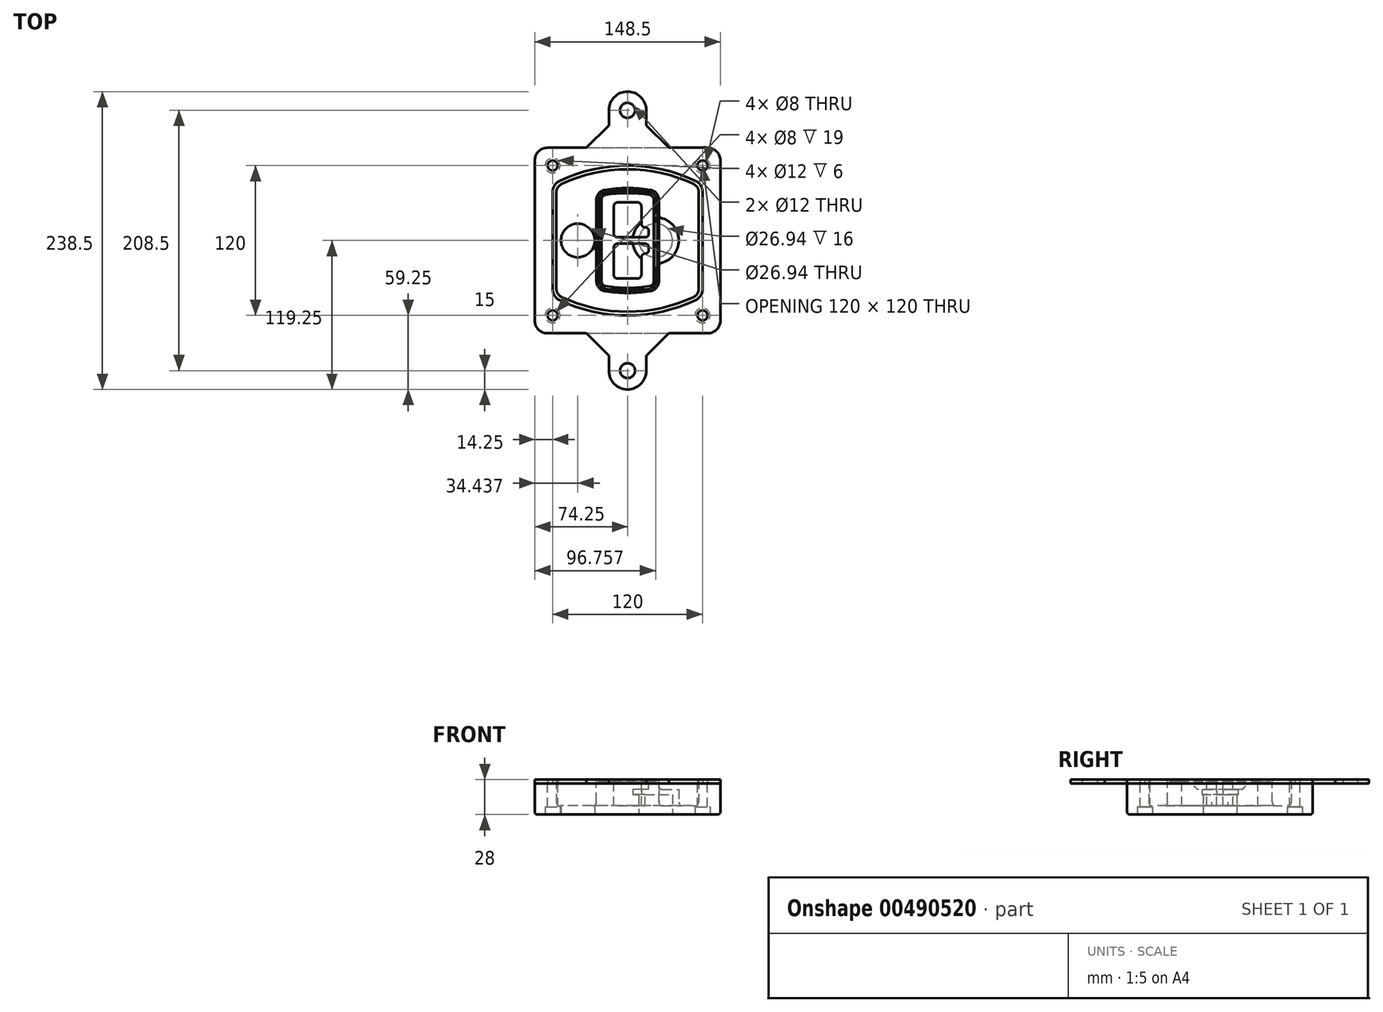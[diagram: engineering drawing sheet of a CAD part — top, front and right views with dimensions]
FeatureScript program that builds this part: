
annotation { "Feature Type Name" : "Feature", "Feature Type Description" : "" }
export const myFeature = defineFeature(function(context is Context, id is Id, definition is map)
    precondition{}
    {
        {
            var Q0;
            Q0=qCreatedBy(makeId("Top.planeOp"),FACE);
            var sketch = newSketch(context, id + "F0", { "sketchPlane" : qUnion([Q0])});
            skPoint(sketch, "E0.rect.middle", {"position": v(0, 0) * mm});
            skLineSegment(sketch, "E1.bottom", {"start": v(-64.25, -74.25) * mm, "end": v(64.25, -74.25) * mm});
            skLineSegment(sketch, "E1.top", {"start": v(-64.25, 74.25) * mm, "end": v(64.25, 74.25) * mm});
            skLineSegment(sketch, "E1.left", {"start": v(-74.25, -64.25) * mm, "end": v(-74.25, 64.25) * mm});
            skLineSegment(sketch, "E1.right", {"start": v(74.25, -64.25) * mm, "end": v(74.25, 64.25) * mm});
            skLineSegment(sketch, "E2", {"start": v(-74.25, 74.25) * mm, "end": v(74.25, -74.25) * mm, "construction": true});
            skLineSegment(sketch, "E3", {"start": v(74.25, 74.25) * mm, "end": v(-74.25, -74.25) * mm, "construction": true});
            skCircle(sketch, "E4", {"center": v(-60, 60) * mm, "radius": 4 * mm});
            skCircle(sketch, "E5", {"center": v(60, 60) * mm, "radius": 4 * mm});
            skCircle(sketch, "E6", {"center": v(60, -60) * mm, "radius": 4 * mm});
            skCircle(sketch, "E7", {"center": v(-60, -60) * mm, "radius": 4 * mm});
            skLineSegment(sketch, "E8", {"start": v(-60, 60) * mm, "end": v(60, 60) * mm, "construction": true});
            skLineSegment(sketch, "E9", {"start": v(60, 60) * mm, "end": v(60, -60) * mm, "construction": true});
            skLineSegment(sketch, "E10", {"start": v(60, -60) * mm, "end": v(-60, -60) * mm, "construction": true});
            skLineSegment(sketch, "E11", {"start": v(-60, -60) * mm, "end": v(-60, 60) * mm, "construction": true});
            skLineSegment(sketch, "E12", {"start": v(-60, 38.83) * mm, "end": v(-60, -38.83) * mm});
            skLineSegment(sketch, "E13", {"start": v(60, 38.83) * mm, "end": v(60, -38.83) * mm});
            skArc(sketch, "E14", {"start": v(54.26, 47.88) * mm, "mid": v(0, 60) * mm, "end": v(-54.26, 47.88) * mm});
            skArc(sketch, "E15", {"start": v(-54.26, -47.88) * mm, "mid": v(0, -60) * mm, "end": v(54.26, -47.88) * mm});
            skLineSegment(sketch, "E16", {"start": v(-60, 0) * mm, "end": v(60, 0) * mm, "construction": true});
            skPoint(sketch, "E17.visualSharp", {"position": v(-60, -45) * mm});
            skArc(sketch, "E17.filletArc", {"start": v(-60, -38.83) * mm, "mid": v(-58.44, -44.2) * mm, "end": v(-54.26, -47.88) * mm});
            skPoint(sketch, "E18.visualSharp", {"position": v(-60, 45) * mm});
            skArc(sketch, "E18.filletArc", {"start": v(-54.26, 47.88) * mm, "mid": v(-58.44, 44.2) * mm, "end": v(-60, 38.83) * mm});
            skPoint(sketch, "E19.visualSharp", {"position": v(60, 45) * mm});
            skArc(sketch, "E19.filletArc", {"start": v(60, 38.83) * mm, "mid": v(58.44, 44.2) * mm, "end": v(54.26, 47.88) * mm});
            skPoint(sketch, "E20.visualSharp", {"position": v(60, -45) * mm});
            skArc(sketch, "E20.filletArc", {"start": v(54.26, -47.88) * mm, "mid": v(58.44, -44.2) * mm, "end": v(60, -38.83) * mm});
            skPoint(sketch, "E21.visualSharp", {"position": v(-74.25, 74.25) * mm});
            skArc(sketch, "E21.filletArc", {"start": v(-64.25, 74.25) * mm, "mid": v(-71.32, 71.32) * mm, "end": v(-74.25, 64.25) * mm});
            skPoint(sketch, "E22.visualSharp", {"position": v(74.25, 74.25) * mm});
            skArc(sketch, "E22.filletArc", {"start": v(74.25, 64.25) * mm, "mid": v(71.32, 71.32) * mm, "end": v(64.25, 74.25) * mm});
            skPoint(sketch, "E23.visualSharp", {"position": v(74.25, -74.25) * mm});
            skArc(sketch, "E23.filletArc", {"start": v(64.25, -74.25) * mm, "mid": v(71.32, -71.32) * mm, "end": v(74.25, -64.25) * mm});
            skPoint(sketch, "E24.visualSharp", {"position": v(-74.25, -74.25) * mm});
            skArc(sketch, "E24.filletArc", {"start": v(-74.25, -64.25) * mm, "mid": v(-71.32, -71.32) * mm, "end": v(-64.25, -74.25) * mm});
            skArc(sketch, "E25.0", {"start": v(57, 38.83) * mm, "mid": v(55.9, 42.58) * mm, "end": v(52.98, 45.17) * mm});
            skLineSegment(sketch, "E25.1", {"start": v(57, 38.83) * mm, "end": v(57, -38.83) * mm});
            skArc(sketch, "E25.2", {"start": v(52.98, -45.17) * mm, "mid": v(55.9, -42.58) * mm, "end": v(57, -38.83) * mm});
            skArc(sketch, "E25.3", {"start": v(-52.98, -45.17) * mm, "mid": v(0, -57) * mm, "end": v(52.98, -45.17) * mm});
            skArc(sketch, "E25.4", {"start": v(-57, -38.83) * mm, "mid": v(-55.9, -42.58) * mm, "end": v(-52.98, -45.17) * mm});
            skArc(sketch, "E25.5", {"start": v(52.98, 45.17) * mm, "mid": v(0, 57) * mm, "end": v(-52.98, 45.17) * mm});
            skLineSegment(sketch, "E25.6", {"start": v(-57, 38.83) * mm, "end": v(-57, -38.83) * mm});
            skArc(sketch, "E25.7", {"start": v(-52.98, 45.17) * mm, "mid": v(-55.9, 42.58) * mm, "end": v(-57, 38.83) * mm});
            skArc(sketch, "E26.0", {"start": v(-55.96, 51.5) * mm, "mid": v(-61.82, 46.33) * mm, "end": v(-64, 38.83) * mm});
            skArc(sketch, "E26.1", {"start": v(55.96, 51.5) * mm, "mid": v(0, 64) * mm, "end": v(-55.96, 51.5) * mm});
            skArc(sketch, "E26.2", {"start": v(64, 38.83) * mm, "mid": v(61.82, 46.33) * mm, "end": v(55.96, 51.5) * mm});
            skLineSegment(sketch, "E26.3", {"start": v(64, 38.83) * mm, "end": v(64, -38.83) * mm});
            skArc(sketch, "E26.4", {"start": v(55.96, -51.5) * mm, "mid": v(61.82, -46.33) * mm, "end": v(64, -38.83) * mm});
            skLineSegment(sketch, "E26.5", {"start": v(-64, 38.83) * mm, "end": v(-64, -38.83) * mm});
            skArc(sketch, "E26.6", {"start": v(-55.96, -51.5) * mm, "mid": v(0, -64) * mm, "end": v(55.96, -51.5) * mm});
            skArc(sketch, "E26.7", {"start": v(-64, -38.83) * mm, "mid": v(-61.82, -46.33) * mm, "end": v(-55.96, -51.5) * mm});
            skSolve(sketch);
        }
        {
            var Q0;
            Q0=makeQuery(id+"F0.imprint","IMPRINT",FACE,{"disambiguationData":[TD([[makeQuery(id+"F0.imprint","IMPRINT",EDGE,{"derivedFrom":sQuery(id+"F0.wireOp",EDGE,"E1.bottom")}),1.0]])]});
            var Q1;
            Q1=makeQuery(id+"F0.imprint","IMPRINT",FACE,{"disambiguationData":[TD([[makeQuery(id+"F0.imprint","IMPRINT",EDGE,{"derivedFrom":sQuery(id+"F0.wireOp",EDGE,"E12")}),1.0]])]});
            var Q2;
            Q2=makeQuery(id+"F0.imprint","IMPRINT",FACE,{"disambiguationData":[TD([[makeQuery(id+"F0.imprint","IMPRINT",EDGE,{"derivedFrom":sQuery(id+"F0.wireOp",EDGE,"E25.0")}),1.0]])]});
            var Q3;
            Q3=makeQuery(id+"F0.imprint","IMPRINT",FACE,{"disambiguationData":[TD([[makeQuery(id+"F0.imprint","IMPRINT",EDGE,{"derivedFrom":sQuery(id+"F0.wireOp",EDGE,"E12")}),-1.0]])]});
            extrude(context, id + "F1", {"entities" : qUnion([Q0, Q1, Q2, Q3]), "oppositeDirection" : true, "depth" : 25 * mm});
        }
        {
            var Q0;
            Q0=makeQuery(id+"F0.imprint","IMPRINT",FACE,{"disambiguationData":[TD([[makeQuery(id+"F0.imprint","IMPRINT",EDGE,{"derivedFrom":sQuery(id+"F0.wireOp",EDGE,"E12")}),1.0]])]});
            extrude(context, id + "F2", {"entities" : qUnion([Q0]), "operationType" : NewBodyOperationType.ADD, "depth" : 3 * mm});
        }
        {
            var Q0;
            Q0=makeQuery(id+"F0.imprint","IMPRINT",FACE,{"disambiguationData":[TD([[makeQuery(id+"F0.imprint","IMPRINT",EDGE,{"derivedFrom":sQuery(id+"F0.wireOp",EDGE,"E25.0")}),1.0]])]});
            extrude(context, id + "F3", {"entities" : qUnion([Q0]), "operationType" : NewBodyOperationType.REMOVE, "oppositeDirection" : true, "depth" : 18 * mm});
        }
        {
            var Q0;
            Q0=makeQuery(id+"F2.opExtrude","CAP_FACE",FACE,{"disambiguationData":[OSD([sQuery(id+"F0.wireOp",EDGE,"E12"),sQuery(id+"F0.wireOp",EDGE,"E13"),sQuery(id+"F0.wireOp",EDGE,"E14"),sQuery(id+"F0.wireOp",EDGE,"E15"),sQuery(id+"F0.wireOp",EDGE,"E17.filletArc"),sQuery(id+"F0.wireOp",EDGE,"E18.filletArc"),sQuery(id+"F0.wireOp",EDGE,"E19.filletArc"),sQuery(id+"F0.wireOp",EDGE,"E20.filletArc"),sQuery(id+"F0.wireOp",EDGE,"E25.0"),sQuery(id+"F0.wireOp",EDGE,"E25.1"),sQuery(id+"F0.wireOp",EDGE,"E25.2"),sQuery(id+"F0.wireOp",EDGE,"E25.3"),sQuery(id+"F0.wireOp",EDGE,"E25.4"),sQuery(id+"F0.wireOp",EDGE,"E25.5"),sQuery(id+"F0.wireOp",EDGE,"E25.6"),sQuery(id+"F0.wireOp",EDGE,"E25.7")])],"isStart":false});
            var sketch = newSketch(context, id + "F4", { "sketchPlane" : qUnion([Q0])});
            skArc(sketch, "E27.0", {"start": v(-18.34, -40.45) * mm, "mid": v(0, -42) * mm, "end": v(18.34, -40.45) * mm});
            skArc(sketch, "E28.0", {"start": v(18.34, 40.45) * mm, "mid": v(0, 42) * mm, "end": v(-18.34, 40.45) * mm});
            skLineSegment(sketch, "E29", {"start": v(-25, 32.57) * mm, "end": v(-25, -32.57) * mm});
            skLineSegment(sketch, "E30", {"start": v(25, 32.57) * mm, "end": v(25, -32.57) * mm});
            skLineSegment(sketch, "E31", {"start": v(-25, 39.1) * mm, "end": v(25, 39.1) * mm, "construction": true});
            skLineSegment(sketch, "E32", {"start": v(-25, -39.1) * mm, "end": v(25, -39.1) * mm, "construction": true});
            skPoint(sketch, "E33.visualSharp", {"position": v(-25, 39.1) * mm});
            skArc(sketch, "E33.filletArc", {"start": v(-18.34, 40.45) * mm, "mid": v(-23.11, 37.73) * mm, "end": v(-25, 32.57) * mm});
            skPoint(sketch, "E34.visualSharp", {"position": v(25, 39.1) * mm});
            skArc(sketch, "E34.filletArc", {"start": v(25, 32.57) * mm, "mid": v(23.11, 37.73) * mm, "end": v(18.34, 40.45) * mm});
            skPoint(sketch, "E35.visualSharp", {"position": v(25, -39.1) * mm});
            skArc(sketch, "E35.filletArc", {"start": v(18.34, -40.45) * mm, "mid": v(23.11, -37.73) * mm, "end": v(25, -32.57) * mm});
            skPoint(sketch, "E36.visualSharp", {"position": v(-25, -39.1) * mm});
            skArc(sketch, "E36.filletArc", {"start": v(-25, -32.57) * mm, "mid": v(-23.11, -37.73) * mm, "end": v(-18.34, -40.45) * mm});
            skArc(sketch, "E37.0", {"start": v(52.98, 45.17) * mm, "mid": v(0, 57) * mm, "end": v(-52.98, 45.17) * mm});
            skArc(sketch, "E37.1", {"start": v(-52.98, 45.17) * mm, "mid": v(-55.9, 42.58) * mm, "end": v(-57, 38.83) * mm});
            skLineSegment(sketch, "E37.2", {"start": v(-57, 38.83) * mm, "end": v(-57, -38.83) * mm});
            skArc(sketch, "E37.3", {"start": v(-57, -38.83) * mm, "mid": v(-55.9, -42.58) * mm, "end": v(-52.98, -45.17) * mm});
            skArc(sketch, "E37.4", {"start": v(-52.98, -45.17) * mm, "mid": v(0, -57) * mm, "end": v(52.98, -45.17) * mm});
            skArc(sketch, "E37.5", {"start": v(52.98, -45.17) * mm, "mid": v(55.9, -42.58) * mm, "end": v(57, -38.83) * mm});
            skLineSegment(sketch, "E37.6", {"start": v(57, 38.83) * mm, "end": v(57, -38.83) * mm});
            skArc(sketch, "E37.7", {"start": v(57, 38.83) * mm, "mid": v(55.9, 42.58) * mm, "end": v(52.98, 45.17) * mm});
            skLineSegment(sketch, "E38.0", {"start": v(23, 32.57) * mm, "end": v(23, -32.57) * mm});
            skArc(sketch, "E38.1", {"start": v(18, -38.48) * mm, "mid": v(21.58, -36.44) * mm, "end": v(23, -32.57) * mm});
            skArc(sketch, "E38.2", {"start": v(-18, -38.48) * mm, "mid": v(0, -40) * mm, "end": v(18, -38.48) * mm});
            skArc(sketch, "E38.3", {"start": v(-23, -32.57) * mm, "mid": v(-21.58, -36.44) * mm, "end": v(-18, -38.48) * mm});
            skLineSegment(sketch, "E38.4", {"start": v(-23, 32.57) * mm, "end": v(-23, -32.57) * mm});
            skArc(sketch, "E38.5", {"start": v(23, 32.57) * mm, "mid": v(21.58, 36.44) * mm, "end": v(18, 38.48) * mm});
            skArc(sketch, "E38.6", {"start": v(-18, 38.48) * mm, "mid": v(-21.58, 36.44) * mm, "end": v(-23, 32.57) * mm});
            skArc(sketch, "E38.7", {"start": v(18, 38.48) * mm, "mid": v(0, 40) * mm, "end": v(-18, 38.48) * mm});
            skArc(sketch, "E39.0", {"start": v(21, 32.57) * mm, "mid": v(20.06, 35.15) * mm, "end": v(17.67, 36.5) * mm});
            skLineSegment(sketch, "E39.1", {"start": v(21, 32.57) * mm, "end": v(21, -32.57) * mm});
            skArc(sketch, "E39.2", {"start": v(17.67, -36.5) * mm, "mid": v(20.06, -35.15) * mm, "end": v(21, -32.57) * mm});
            skArc(sketch, "E39.3", {"start": v(-17.67, -36.5) * mm, "mid": v(0, -38) * mm, "end": v(17.67, -36.5) * mm});
            skArc(sketch, "E39.4", {"start": v(-21, -32.57) * mm, "mid": v(-20.06, -35.15) * mm, "end": v(-17.67, -36.5) * mm});
            skArc(sketch, "E39.5", {"start": v(17.67, 36.5) * mm, "mid": v(0, 38) * mm, "end": v(-17.67, 36.5) * mm});
            skLineSegment(sketch, "E39.6", {"start": v(-21, 32.57) * mm, "end": v(-21, -32.57) * mm});
            skArc(sketch, "E39.7", {"start": v(-17.67, 36.5) * mm, "mid": v(-20.06, 35.15) * mm, "end": v(-21, 32.57) * mm});
            skLineSegment(sketch, "E40", {"start": v(-25, 0) * mm, "end": v(25, 0) * mm, "construction": true});
            skLineSegment(sketch, "E41", {"start": v(-11, 5.5) * mm, "end": v(-11, 27.5) * mm});
            skLineSegment(sketch, "E42", {"start": v(-8, 30.5) * mm, "end": v(8, 30.5) * mm});
            skLineSegment(sketch, "E43", {"start": v(11, 27.5) * mm, "end": v(11, 13.5) * mm});
            skLineSegment(sketch, "E44", {"start": v(14, 10.5) * mm, "end": v(14, 10.5) * mm});
            skLineSegment(sketch, "E45", {"start": v(17, 7.5) * mm, "end": v(17, 5.5) * mm});
            skLineSegment(sketch, "E46", {"start": v(14, 2.5) * mm, "end": v(-8, 2.5) * mm});
            skPoint(sketch, "E47.visualSharp", {"position": v(-11, 30.5) * mm});
            skArc(sketch, "E47.filletArc", {"start": v(-8, 30.5) * mm, "mid": v(-10.12, 29.62) * mm, "end": v(-11, 27.5) * mm});
            skPoint(sketch, "E48.visualSharp", {"position": v(11, 30.5) * mm});
            skArc(sketch, "E48.filletArc", {"start": v(11, 27.5) * mm, "mid": v(10.12, 29.62) * mm, "end": v(8, 30.5) * mm});
            skPoint(sketch, "E49.visualSharp", {"position": v(11, 10.5) * mm});
            skArc(sketch, "E49.filletArc", {"start": v(11, 13.5) * mm, "mid": v(11.88, 11.38) * mm, "end": v(14, 10.5) * mm});
            skPoint(sketch, "E50.visualSharp", {"position": v(17, 10.5) * mm});
            skArc(sketch, "E50.filletArc", {"start": v(17, 7.5) * mm, "mid": v(16.12, 9.62) * mm, "end": v(14, 10.5) * mm});
            skPoint(sketch, "E51.visualSharp", {"position": v(17, 2.5) * mm});
            skArc(sketch, "E51.filletArc", {"start": v(14, 2.5) * mm, "mid": v(16.12, 3.38) * mm, "end": v(17, 5.5) * mm});
            skPoint(sketch, "E52.visualSharp", {"position": v(-11, 2.5) * mm});
            skArc(sketch, "E52.filletArc", {"start": v(-11, 5.5) * mm, "mid": v(-10.12, 3.38) * mm, "end": v(-8, 2.5) * mm});
            skLineSegment(sketch, "E53.0.MirrorCS", {"start": v(14, -2.5) * mm, "end": v(-8, -2.5) * mm});
            skArc(sketch, "E54.0.MirrorCS", {"start": v(-11, -5.5) * mm, "mid": v(-10.12, -3.38) * mm, "end": v(-8, -2.5) * mm});
            skLineSegment(sketch, "E55.0.MirrorCS", {"start": v(-11, -5.5) * mm, "end": v(-11, -27.5) * mm});
            skArc(sketch, "E56.0.MirrorCS", {"start": v(-8, -30.5) * mm, "mid": v(-10.12, -29.62) * mm, "end": v(-11, -27.5) * mm});
            skLineSegment(sketch, "E57.0.MirrorCS", {"start": v(-8, -30.5) * mm, "end": v(8, -30.5) * mm});
            skArc(sketch, "E58.0.MirrorCS", {"start": v(11, -27.5) * mm, "mid": v(10.12, -29.62) * mm, "end": v(8, -30.5) * mm});
            skLineSegment(sketch, "E59.0.MirrorCS", {"start": v(11, -27.5) * mm, "end": v(11, -13.5) * mm});
            skArc(sketch, "E60.0.MirrorCS", {"start": v(11, -13.5) * mm, "mid": v(11.88, -11.38) * mm, "end": v(14, -10.5) * mm});
            skArc(sketch, "E61.0.MirrorCS", {"start": v(17, -7.5) * mm, "mid": v(16.12, -9.62) * mm, "end": v(14, -10.5) * mm});
            skLineSegment(sketch, "E62.0.MirrorCS", {"start": v(17, -7.5) * mm, "end": v(17, -5.5) * mm});
            skArc(sketch, "E63.0.MirrorCS", {"start": v(14, -2.5) * mm, "mid": v(16.12, -3.38) * mm, "end": v(17, -5.5) * mm});
            skSolve(sketch);
        }
        {
            var Q0;
            Q0=makeQuery(id+"F4.imprint","IMPRINT",FACE,{"disambiguationData":[TD([[makeQuery(id+"F4.imprint","IMPRINT",EDGE,{"derivedFrom":sQuery(id+"F4.wireOp",EDGE,"E27.0")}),1.0]])]});
            var Q1;
            Q1=makeQuery(id+"F4.imprint","IMPRINT",FACE,{"disambiguationData":[TD([[makeQuery(id+"F4.imprint","IMPRINT",EDGE,{"derivedFrom":sQuery(id+"F4.wireOp",EDGE,"E38.0")}),-1.0]])]});
            var Q2;
            Q2=makeQuery(id+"F4.imprint","IMPRINT",FACE,{"disambiguationData":[TD([[makeQuery(id+"F4.imprint","IMPRINT",EDGE,{"derivedFrom":sQuery(id+"F4.wireOp",EDGE,"E39.0")}),1.0]])]});
            extrude(context, id + "F5", {"entities" : qUnion([Q0, Q1, Q2]), "operationType" : NewBodyOperationType.ADD, "endBound" : BoundingType.UP_TO_NEXT, "oppositeDirection" : true, "depth" : 25 * mm});
        }
        {
            var Q0;
            Q0=makeQuery(id+"F4.imprint","IMPRINT",FACE,{"disambiguationData":[TD([[makeQuery(id+"F4.imprint","IMPRINT",EDGE,{"derivedFrom":sQuery(id+"F4.wireOp",EDGE,"E38.0")}),-1.0]])]});
            extrude(context, id + "F6", {"entities" : qUnion([Q0]), "operationType" : NewBodyOperationType.REMOVE, "oppositeDirection" : true, "depth" : 2 * mm});
        }
        {
            var Q0;
            Q0=makeQuery(id+"F1.opExtrude","CAP_FACE",FACE,{"disambiguationData":[OSD([sQuery(id+"F0.wireOp",EDGE,"E1.bottom"),sQuery(id+"F0.wireOp",EDGE,"E1.top"),sQuery(id+"F0.wireOp",EDGE,"E1.left"),sQuery(id+"F0.wireOp",EDGE,"E1.right"),sQuery(id+"F0.wireOp",EDGE,"E4"),sQuery(id+"F0.wireOp",EDGE,"E5"),sQuery(id+"F0.wireOp",EDGE,"E6"),sQuery(id+"F0.wireOp",EDGE,"E7"),sQuery(id+"F0.wireOp",EDGE,"E21.filletArc"),sQuery(id+"F0.wireOp",EDGE,"E22.filletArc"),sQuery(id+"F0.wireOp",EDGE,"E23.filletArc"),sQuery(id+"F0.wireOp",EDGE,"E24.filletArc")])],"isStart":false});
            var sketch = newSketch(context, id + "F7", { "sketchPlane" : qUnion([Q0])});
            skCircle(sketch, "E64", {"center": v(22.5, 0) * mm, "radius": 13.47 * mm});
            skCircle(sketch, "E65", {"center": v(-39.81, 0) * mm, "radius": 13.47 * mm});
            skLineSegment(sketch, "E66", {"start": v(74.25, 0) * mm, "end": v(-74.25, 0) * mm});
            skCircle(sketch, "E67", {"center": v(22.5, 0) * mm, "radius": 18.47 * mm});
            skCircle(sketch, "E68", {"center": v(60, -60) * mm, "radius": 6 * mm});
            skCircle(sketch, "E69", {"center": v(-60, -60) * mm, "radius": 6 * mm});
            skCircle(sketch, "E70", {"center": v(-60, 60) * mm, "radius": 6 * mm});
            skCircle(sketch, "E71", {"center": v(60, 60) * mm, "radius": 6 * mm});
            skSolve(sketch);
        }
        {
            var Q0;
            {var subQ1=sQuery(id+"F7.wireOp",EDGE,"E66");var subQ4=sQuery(id+"F7.wireOp",EDGE,"E64");var subQ6=makeQuery(id+"F7.imprint","INTERSECT",VERTEX,{"disambiguationData":[OD(0.0)],"derivedFrom":[subQ4,subQ1]});Q0=makeQuery(id+"F7.imprint","IMPRINT",FACE,{"disambiguationData":[TD([[makeQuery(id+"F7.imprint","IMPRINT",EDGE,{"disambiguationData":[TD([[subQ6,-1.0]])],"derivedFrom":subQ4}),-1.0]])]});}
            var Q1;
            {var subQ0=sQuery(id+"F7.wireOp",EDGE,"E66");var subQ1=sQuery(id+"F7.wireOp",EDGE,"E64");var subQ3=makeQuery(id+"F7.imprint","INTERSECT",VERTEX,{"disambiguationData":[OD(0.0)],"derivedFrom":[subQ1,subQ0]});Q1=makeQuery(id+"F7.imprint","IMPRINT",FACE,{"disambiguationData":[TD([[makeQuery(id+"F7.imprint","IMPRINT",EDGE,{"disambiguationData":[TD([[subQ3,-1.0]])],"derivedFrom":subQ1}),1.0]])]});}
            var Q2;
            {var subQ0=sQuery(id+"F7.wireOp",EDGE,"E66");var subQ1=sQuery(id+"F7.wireOp",EDGE,"E64");var subQ3=makeQuery(id+"F7.imprint","INTERSECT",VERTEX,{"disambiguationData":[OD(0.0)],"derivedFrom":[subQ1,subQ0]});Q2=makeQuery(id+"F7.imprint","IMPRINT",FACE,{"disambiguationData":[TD([[makeQuery(id+"F7.imprint","IMPRINT",EDGE,{"disambiguationData":[TD([[subQ3,1.0]])],"derivedFrom":subQ1}),1.0]])]});}
            var Q3;
            {var subQ1=sQuery(id+"F7.wireOp",EDGE,"E66");var subQ4=sQuery(id+"F7.wireOp",EDGE,"E64");var subQ6=makeQuery(id+"F7.imprint","INTERSECT",VERTEX,{"disambiguationData":[OD(0.0)],"derivedFrom":[subQ4,subQ1]});Q3=makeQuery(id+"F7.imprint","IMPRINT",FACE,{"disambiguationData":[TD([[makeQuery(id+"F7.imprint","IMPRINT",EDGE,{"disambiguationData":[TD([[subQ6,1.0]])],"derivedFrom":subQ4}),-1.0]])]});}
            extrude(context, id + "F8", {"entities" : qUnion([Q0, Q1, Q2, Q3]), "operationType" : NewBodyOperationType.ADD, "oppositeDirection" : true, "depth" : 20 * mm});
        }
        {
            var Q0;
            {var subQ0=sQuery(id+"F7.wireOp",EDGE,"E66");var subQ1=sQuery(id+"F7.wireOp",EDGE,"E64");var subQ3=makeQuery(id+"F7.imprint","INTERSECT",VERTEX,{"disambiguationData":[OD(0.0)],"derivedFrom":[subQ1,subQ0]});Q0=makeQuery(id+"F7.imprint","IMPRINT",FACE,{"disambiguationData":[TD([[makeQuery(id+"F7.imprint","IMPRINT",EDGE,{"disambiguationData":[TD([[subQ3,-1.0]])],"derivedFrom":subQ1}),1.0]])]});}
            var Q1;
            {var subQ0=sQuery(id+"F7.wireOp",EDGE,"E66");var subQ1=sQuery(id+"F7.wireOp",EDGE,"E64");var subQ3=makeQuery(id+"F7.imprint","INTERSECT",VERTEX,{"disambiguationData":[OD(0.0)],"derivedFrom":[subQ1,subQ0]});Q1=makeQuery(id+"F7.imprint","IMPRINT",FACE,{"disambiguationData":[TD([[makeQuery(id+"F7.imprint","IMPRINT",EDGE,{"disambiguationData":[TD([[subQ3,1.0]])],"derivedFrom":subQ1}),1.0]])]});}
            extrude(context, id + "F9", {"entities" : qUnion([Q0, Q1]), "operationType" : NewBodyOperationType.REMOVE, "oppositeDirection" : true, "depth" : 16 * mm});
        }
        {
            var Q0;
            {var subQ0=sQuery(id+"F7.wireOp",EDGE,"E66");var subQ1=sQuery(id+"F7.wireOp",EDGE,"E65");var subQ3=makeQuery(id+"F7.imprint","INTERSECT",VERTEX,{"disambiguationData":[OD(0.0)],"derivedFrom":[subQ1,subQ0]});Q0=makeQuery(id+"F7.imprint","IMPRINT",FACE,{"disambiguationData":[TD([[makeQuery(id+"F7.imprint","IMPRINT",EDGE,{"disambiguationData":[TD([[subQ3,-1.0]])],"derivedFrom":subQ1}),1.0]])]});}
            var Q1;
            {var subQ0=sQuery(id+"F7.wireOp",EDGE,"E66");var subQ1=sQuery(id+"F7.wireOp",EDGE,"E65");var subQ3=makeQuery(id+"F7.imprint","INTERSECT",VERTEX,{"disambiguationData":[OD(0.0)],"derivedFrom":[subQ1,subQ0]});Q1=makeQuery(id+"F7.imprint","IMPRINT",FACE,{"disambiguationData":[TD([[makeQuery(id+"F7.imprint","IMPRINT",EDGE,{"disambiguationData":[TD([[subQ3,1.0]])],"derivedFrom":subQ1}),1.0]])]});}
            extrude(context, id + "F10", {"entities" : qUnion([Q0, Q1]), "operationType" : NewBodyOperationType.REMOVE, "oppositeDirection" : true, "depth" : 25 * mm});
        }
        {
            var Q0;
            Q0=makeQuery(id+"F7.imprint","IMPRINT",FACE,{"disambiguationData":[TD([[makeQuery(id+"F7.imprint","IMPRINT",EDGE,{"derivedFrom":sQuery(id+"F7.wireOp",EDGE,"E68")}),1.0]])]});
            var Q1;
            Q1=makeQuery(id+"F7.imprint","IMPRINT",FACE,{"disambiguationData":[TD([[makeQuery(id+"F7.imprint","IMPRINT",EDGE,{"derivedFrom":makeQuery(id+"F1.opExtrude","CAP_EDGE",EDGE,{"disambiguationData":[OSD([sQuery(id+"F0.wireOp",EDGE,"E5")])],"isStart":false})}),-1.0]])]});
            var Q2;
            Q2=makeQuery(id+"F7.imprint","IMPRINT",FACE,{"disambiguationData":[TD([[makeQuery(id+"F7.imprint","IMPRINT",EDGE,{"derivedFrom":sQuery(id+"F7.wireOp",EDGE,"E69")}),1.0]])]});
            var Q3;
            Q3=makeQuery(id+"F7.imprint","IMPRINT",FACE,{"disambiguationData":[TD([[makeQuery(id+"F7.imprint","IMPRINT",EDGE,{"derivedFrom":makeQuery(id+"F1.opExtrude","CAP_EDGE",EDGE,{"disambiguationData":[OSD([sQuery(id+"F0.wireOp",EDGE,"E4")])],"isStart":false})}),-1.0]])]});
            var Q4;
            Q4=makeQuery(id+"F7.imprint","IMPRINT",FACE,{"disambiguationData":[TD([[makeQuery(id+"F7.imprint","IMPRINT",EDGE,{"derivedFrom":sQuery(id+"F7.wireOp",EDGE,"E70")}),1.0]])]});
            var Q5;
            Q5=makeQuery(id+"F7.imprint","IMPRINT",FACE,{"disambiguationData":[TD([[makeQuery(id+"F7.imprint","IMPRINT",EDGE,{"derivedFrom":makeQuery(id+"F1.opExtrude","CAP_EDGE",EDGE,{"disambiguationData":[OSD([sQuery(id+"F0.wireOp",EDGE,"E7")])],"isStart":false})}),-1.0]])]});
            var Q6;
            Q6=makeQuery(id+"F7.imprint","IMPRINT",FACE,{"disambiguationData":[TD([[makeQuery(id+"F7.imprint","IMPRINT",EDGE,{"derivedFrom":sQuery(id+"F7.wireOp",EDGE,"E71")}),1.0]])]});
            var Q7;
            Q7=makeQuery(id+"F7.imprint","IMPRINT",FACE,{"disambiguationData":[TD([[makeQuery(id+"F7.imprint","IMPRINT",EDGE,{"derivedFrom":makeQuery(id+"F1.opExtrude","CAP_EDGE",EDGE,{"disambiguationData":[OSD([sQuery(id+"F0.wireOp",EDGE,"E6")])],"isStart":false})}),-1.0]])]});
            extrude(context, id + "F11", {"entities" : qUnion([Q0, Q1, Q2, Q3, Q4, Q5, Q6, Q7]), "operationType" : NewBodyOperationType.REMOVE, "oppositeDirection" : true, "depth" : 6 * mm});
        }
        {
            var Q0;
            Q0=makeQuery(id+"F9.boolean.opBoolean","COPY",FACE,{"derivedFrom":makeQuery(id+"F9.opExtrude","CAP_FACE",FACE,{"disambiguationData":[OSD([sQuery(id+"F7.wireOp",EDGE,"E64")])],"isStart":false})});
            var sketch = newSketch(context, id + "F12", { "sketchPlane" : qUnion([Q0])});
            skArc(sketch, "E72.0", {"start": v(11, 14.45) * mm, "mid": v(6.45, 9.13) * mm, "end": v(4.2, 2.5) * mm});
            skArc(sketch, "E72.1", {"start": v(4.2, -2.5) * mm, "mid": v(6.45, -9.13) * mm, "end": v(11, -14.45) * mm});
            skLineSegment(sketch, "E73", {"start": v(4.2, -2.5) * mm, "end": v(14, -2.5) * mm});
            skLineSegment(sketch, "E74.0", {"start": v(14, 2.5) * mm, "end": v(4.2, 2.5) * mm});
            skArc(sketch, "E74.1", {"start": v(14, 2.5) * mm, "mid": v(16.12, 3.38) * mm, "end": v(17, 5.5) * mm});
            skLineSegment(sketch, "E74.2", {"start": v(17, 7.5) * mm, "end": v(17, 5.5) * mm});
            skArc(sketch, "E74.3", {"start": v(17, 7.5) * mm, "mid": v(16.12, 9.62) * mm, "end": v(14, 10.5) * mm});
            skArc(sketch, "E74.4", {"start": v(11, 13.5) * mm, "mid": v(11.88, 11.38) * mm, "end": v(14, 10.5) * mm});
            skLineSegment(sketch, "E74.5", {"start": v(11, 14.45) * mm, "end": v(11, 13.5) * mm});
            skLineSegment(sketch, "E74.7", {"start": v(14, -2.5) * mm, "end": v(4.2, -2.5) * mm});
            skArc(sketch, "E74.8", {"start": v(14, -2.5) * mm, "mid": v(16.12, -3.38) * mm, "end": v(17, -5.5) * mm});
            skLineSegment(sketch, "E74.9", {"start": v(17, -7.5) * mm, "end": v(17, -5.5) * mm});
            skArc(sketch, "E74.10", {"start": v(17, -7.5) * mm, "mid": v(16.12, -9.62) * mm, "end": v(14, -10.5) * mm});
            skArc(sketch, "E74.11", {"start": v(11, -13.5) * mm, "mid": v(11.88, -11.38) * mm, "end": v(14, -10.5) * mm});
            skLineSegment(sketch, "E74.12", {"start": v(11, -14.45) * mm, "end": v(11, -13.5) * mm});
            skPoint(sketch, "E75.orphan", {"position": v(11, -27.5) * mm});
            skPoint(sketch, "E76.orphan", {"position": v(-8, -2.5) * mm});
            skPoint(sketch, "E77.orphan", {"position": v(-8, 2.5) * mm});
            skPoint(sketch, "E78.orphan", {"position": v(11, 27.5) * mm});
            skSolve(sketch);
        }
        {
            var Q0;
            {var subQ7=sQuery(id+"F12.wireOp",EDGE,"E72.0");var subQ14=sQuery(id+"F12.wireOp",EDGE,"E72.1");var subQ16=sQuery(id+"F12.wireOp",EDGE,"E74.1");var subQ18=sQuery(id+"F12.wireOp",EDGE,"E74.8");Q0=qUnion([makeQuery(id+"F12.imprint","IMPRINT",FACE,{"disambiguationData":[TD([[makeQuery(id+"F12.imprint","IMPRINT",EDGE,{"derivedFrom":subQ7}),1.0]])]}),makeQuery(id+"F12.imprint","IMPRINT",FACE,{"disambiguationData":[TD([[makeQuery(id+"F12.imprint","IMPRINT",EDGE,{"derivedFrom":subQ14}),1.0]])]}),makeQuery(id+"F12.imprint","IMPRINT",FACE,{"disambiguationData":[TD([[makeQuery(id+"F12.imprint","IMPRINT",EDGE,{"derivedFrom":subQ16}),1.0]])]}),makeQuery(id+"F12.imprint","IMPRINT",FACE,{"disambiguationData":[TD([[makeQuery(id+"F12.imprint","IMPRINT",EDGE,{"derivedFrom":subQ18}),-1.0]])]})]);}
            var Q1;
            Q1=makeQuery(id+"F5.boolean.opBoolean","SPLIT",FACE,{"disambiguationData":[TD([makeQuery(id+"F5.opExtrude","SWEPT_FACE",FACE,{"disambiguationData":[OSD([sQuery(id+"F4.wireOp",EDGE,"E41")])]})])],"derivedFrom":makeQuery(id+"F3.boolean.opBoolean","COPY",FACE,{"derivedFrom":makeQuery(id+"F3.opExtrude","CAP_FACE",FACE,{"disambiguationData":[OSD([sQuery(id+"F0.wireOp",EDGE,"E25.0"),sQuery(id+"F0.wireOp",EDGE,"E25.1"),sQuery(id+"F0.wireOp",EDGE,"E25.2"),sQuery(id+"F0.wireOp",EDGE,"E25.3"),sQuery(id+"F0.wireOp",EDGE,"E25.4"),sQuery(id+"F0.wireOp",EDGE,"E25.5"),sQuery(id+"F0.wireOp",EDGE,"E25.6"),sQuery(id+"F0.wireOp",EDGE,"E25.7")])],"isStart":false})})});
            extrude(context, id + "F13", {"entities" : qUnion([Q0]), "operationType" : NewBodyOperationType.REMOVE, "endBound" : BoundingType.UP_TO_SURFACE, "endBoundEntityFace" : qUnion([Q1]), "depth" : 25 * mm});
        }
        {
            var Q0;
            Q0=makeQuery(id+"F3.boolean.opBoolean","COPY",EDGE,{"derivedFrom":makeQuery(id+"F3.opExtrude","CAP_EDGE",EDGE,{"disambiguationData":[OSD([sQuery(id+"F0.wireOp",EDGE,"E25.6")])],"isStart":false})});
            var Q1;
            Q1=makeQuery(id+"F8.boolean.opBoolean","INTERSECT",EDGE,{"derivedFrom":[makeQuery(id+"F5.opExtrude","SWEPT_FACE",FACE,{"disambiguationData":[OSD([sQuery(id+"F4.wireOp",EDGE,"E30")])]}),makeQuery(id+"F8.opExtrude","CAP_FACE",FACE,{"disambiguationData":[OSD([sQuery(id+"F7.wireOp",EDGE,"E67")])],"isStart":false})]});
            var Q2;
            Q2=makeQuery(id+"F8.boolean.opBoolean","INTERSECT",EDGE,{"disambiguationData":[OD(1.0)],"derivedFrom":[makeQuery(id+"F5.opExtrude","SWEPT_FACE",FACE,{"disambiguationData":[OSD([sQuery(id+"F4.wireOp",EDGE,"E30")])]}),makeQuery(id+"F8.opExtrude","SWEPT_FACE",FACE,{"disambiguationData":[OSD([sQuery(id+"F7.wireOp",EDGE,"E67")])]})]});
            var Q3;
            {var subQ0=sQuery(id+"F4.wireOp",EDGE,"E30");Q3=makeQuery(id+"F8.boolean.opBoolean","SPLIT",EDGE,{"disambiguationData":[TD([makeQuery(id+"F5.opExtrude","SWEPT_FACE",FACE,{"disambiguationData":[OSD([sQuery(id+"F4.wireOp",EDGE,"E35.filletArc")])]})])],"derivedFrom":makeQuery(id+"F5.opExtrude","CAP_EDGE",EDGE,{"disambiguationData":[OSD([subQ0])],"isStart":false})});}
            var Q4;
            {var subQ0=sQuery(id+"F0.wireOp",EDGE,"E25.7");var subQ1=sQuery(id+"F0.wireOp",EDGE,"E25.1");var subQ2=sQuery(id+"F0.wireOp",EDGE,"E25.6");var subQ3=sQuery(id+"F0.wireOp",EDGE,"E25.5");var subQ4=sQuery(id+"F0.wireOp",EDGE,"E25.4");var subQ5=sQuery(id+"F0.wireOp",EDGE,"E25.0");var subQ6=sQuery(id+"F0.wireOp",EDGE,"E25.2");var subQ7=sQuery(id+"F0.wireOp",EDGE,"E25.3");Q4=makeQuery(id+"F8.boolean.opBoolean","INTERSECT",EDGE,{"derivedFrom":[makeQuery(id+"F5.boolean.opBoolean","SPLIT",FACE,{"disambiguationData":[TD([makeQuery(id+"F2.opExtrude","SWEPT_FACE",FACE,{"disambiguationData":[OSD([subQ5])]})])],"derivedFrom":makeQuery(id+"F3.boolean.opBoolean","COPY",FACE,{"derivedFrom":makeQuery(id+"F3.opExtrude","CAP_FACE",FACE,{"disambiguationData":[OSD([subQ5,subQ1,subQ6,subQ7,subQ4,subQ3,subQ2,subQ0])],"isStart":false})})}),makeQuery(id+"F8.opExtrude","SWEPT_FACE",FACE,{"disambiguationData":[OSD([sQuery(id+"F7.wireOp",EDGE,"E67")])]})]});}
            var Q5;
            Q5=makeQuery(id+"F8.boolean.opBoolean","INTERSECT",EDGE,{"disambiguationData":[OD(0.0)],"derivedFrom":[makeQuery(id+"F5.opExtrude","SWEPT_FACE",FACE,{"disambiguationData":[OSD([sQuery(id+"F4.wireOp",EDGE,"E30")])]}),makeQuery(id+"F8.opExtrude","SWEPT_FACE",FACE,{"disambiguationData":[OSD([sQuery(id+"F7.wireOp",EDGE,"E67")])]})]});
            fillet(context, id + "F14", {"entities" : qUnion([Q0, Q1, Q2, Q3, Q4, Q5]), "radius" : 3 * mm, "tangentPropagation" : true, "allowEdgeOverflow" : false});
        }
        {
            var Q0;
            Q0=makeQuery(id+"F1.opExtrude","CAP_EDGE",EDGE,{"disambiguationData":[OSD([sQuery(id+"F0.wireOp",EDGE,"E1.bottom")])],"isStart":false});
            fillet(context, id + "F15", {"entities" : qUnion([Q0]), "radius" : 2 * mm, "tangentPropagation" : true, "allowEdgeOverflow" : false});
        }
        {
            var Q0;
            {var subQ0=sQuery(id+"F0.wireOp",EDGE,"E21.filletArc");var subQ1=sQuery(id+"F0.wireOp",EDGE,"E7");var subQ2=sQuery(id+"F0.wireOp",EDGE,"E6");var subQ3=sQuery(id+"F0.wireOp",EDGE,"E5");var subQ4=sQuery(id+"F0.wireOp",EDGE,"E4");var subQ5=sQuery(id+"F0.wireOp",EDGE,"E22.filletArc");var subQ6=sQuery(id+"F0.wireOp",EDGE,"E1.bottom");var subQ7=sQuery(id+"F0.wireOp",EDGE,"E1.right");var subQ8=sQuery(id+"F0.wireOp",EDGE,"E1.top");var subQ9=sQuery(id+"F0.wireOp",EDGE,"E1.left");var subQ10=sQuery(id+"F0.wireOp",EDGE,"E23.filletArc");var subQ11=sQuery(id+"F0.wireOp",EDGE,"E24.filletArc");Q0=makeQuery(id+"F2.boolean.opBoolean","SPLIT",FACE,{"disambiguationData":[TD([makeQuery(id+"F1.opExtrude","SWEPT_FACE",FACE,{"disambiguationData":[OSD([subQ6])]})])],"derivedFrom":makeQuery(id+"F1.opExtrude","CAP_FACE",FACE,{"disambiguationData":[OSD([subQ6,subQ8,subQ9,subQ7,subQ4,subQ3,subQ2,subQ1,subQ0,subQ5,subQ10,subQ11])],"isStart":true})});}
            var sketch = newSketch(context, id + "F16", { "sketchPlane" : qUnion([Q0])});
            skLineSegment(sketch, "E79", {"start": v(0, 74.25) * mm, "end": v(0, 104.25) * mm, "construction": true});
            skArc(sketch, "E80", {"start": v(15, 104.25) * mm, "mid": v(0, 119.25) * mm, "end": v(-15, 104.25) * mm});
            skLineSegment(sketch, "E81", {"start": v(15, 104.25) * mm, "end": v(15, 92.25) * mm});
            skLineSegment(sketch, "E82", {"start": v(-15, 104.25) * mm, "end": v(-15, 92.25) * mm});
            skLineSegment(sketch, "E83", {"start": v(-15, 92.25) * mm, "end": v(-33, 74.25) * mm});
            skLineSegment(sketch, "E84", {"start": v(15, 92.25) * mm, "end": v(33, 74.25) * mm});
            skCircle(sketch, "E85", {"center": v(0, 104.25) * mm, "radius": 6 * mm});
            skLineSegment(sketch, "E86", {"start": v(-74.25, 0) * mm, "end": v(74.25, 0) * mm, "construction": true});
            skLineSegment(sketch, "E87.MirrorCS", {"start": v(0, -74.25) * mm, "end": v(0, -104.25) * mm, "construction": true});
            skLineSegment(sketch, "E88.MirrorCS", {"start": v(15, -104.25) * mm, "end": v(15, -92.25) * mm});
            skLineSegment(sketch, "E89.MirrorCS", {"start": v(-15, -104.25) * mm, "end": v(-15, -92.25) * mm});
            skArc(sketch, "E90.MirrorCS", {"start": v(15, -104.25) * mm, "mid": v(0, -119.25) * mm, "end": v(-15, -104.25) * mm});
            skLineSegment(sketch, "E91.MirrorCS", {"start": v(-15, -92.25) * mm, "end": v(-33, -74.25) * mm});
            skLineSegment(sketch, "E92.MirrorCS", {"start": v(15, -92.25) * mm, "end": v(33, -74.25) * mm});
            skCircle(sketch, "E93.MirrorC", {"center": v(0, -104.25) * mm, "radius": 6 * mm});
            skSolve(sketch);
        }
        {
            var Q0;
            Q0=makeQuery(id+"F16.imprint","IMPRINT",FACE,{"disambiguationData":[TD([[makeQuery(id+"F16.imprint","IMPRINT",EDGE,{"derivedFrom":sQuery(id+"F16.wireOp",EDGE,"E80")}),1.0]])]});
            var Q1;
            Q1=makeQuery(id+"F16.imprint","IMPRINT",FACE,{"disambiguationData":[TD([[makeQuery(id+"F16.imprint","IMPRINT",EDGE,{"derivedFrom":makeQuery(id+"F1.opExtrude","CAP_EDGE",EDGE,{"disambiguationData":[OSD([sQuery(id+"F0.wireOp",EDGE,"E1.left")])],"isStart":true})}),-1.0]])]});
            var Q2;
            Q2=makeQuery(id+"F16.imprint","IMPRINT",FACE,{"disambiguationData":[TD([[makeQuery(id+"F16.imprint","IMPRINT",EDGE,{"derivedFrom":sQuery(id+"F16.wireOp",EDGE,"E88.MirrorCS")}),1.0]])]});
            var Q3;
            Q3=makeQuery(id+"F2.opExtrude","CAP_FACE",FACE,{"disambiguationData":[OSD([sQuery(id+"F0.wireOp",EDGE,"E12"),sQuery(id+"F0.wireOp",EDGE,"E13"),sQuery(id+"F0.wireOp",EDGE,"E14"),sQuery(id+"F0.wireOp",EDGE,"E15"),sQuery(id+"F0.wireOp",EDGE,"E17.filletArc"),sQuery(id+"F0.wireOp",EDGE,"E18.filletArc"),sQuery(id+"F0.wireOp",EDGE,"E19.filletArc"),sQuery(id+"F0.wireOp",EDGE,"E20.filletArc"),sQuery(id+"F0.wireOp",EDGE,"E25.0"),sQuery(id+"F0.wireOp",EDGE,"E25.1"),sQuery(id+"F0.wireOp",EDGE,"E25.2"),sQuery(id+"F0.wireOp",EDGE,"E25.3"),sQuery(id+"F0.wireOp",EDGE,"E25.4"),sQuery(id+"F0.wireOp",EDGE,"E25.5"),sQuery(id+"F0.wireOp",EDGE,"E25.6"),sQuery(id+"F0.wireOp",EDGE,"E25.7")])],"isStart":false});
            extrude(context, id + "F17", {"entities" : qUnion([Q0, Q1, Q2]), "endBound" : BoundingType.UP_TO_SURFACE, "endBoundEntityFace" : qUnion([Q3]), "depth" : 25 * mm});
        }
    });
